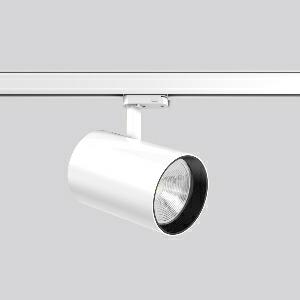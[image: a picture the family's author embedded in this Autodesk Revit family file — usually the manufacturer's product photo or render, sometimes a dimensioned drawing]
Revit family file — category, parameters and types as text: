
# Revit family: deecos_s_maxi_742231_002_76_5936
name_source: partatom
category: Lighting Fixtures
units: mm (PartAtom-declared; Revit-internal decimal feet)

## family parameters
Cut with Voids When Loaded = No
Host = Face
Light Source = No
Part Type = Normal
Room Calculation Point = No
Round Connector Dimension = Use Diameter
Shared = No

## types (1)
- DEECOS S maxi (1 x LED Modul 932 fresh meat, 1800 lm, 3200)
    Apparent Load = 33 VA
    Approval mark = CE
    CIE Flux Codes = 97 100 100 100 100
    Color Rendering = 90
    Color Temperature = 3200
    Default Elevation = 1800 mm  [stored 5.90551 ft]
    Description = Series: DEECOS S maxi
LED surface-mounted projector in modern design with no visible cooling ribs. Housing: die-cast aluminium, powder-coated. Rotation range: 356°. Swivel range: 90°. Black plastic ring and recessed LED to prevent glare from the side. Optical assembly with lens made of plastic (polycarbonate) for the best homogeneous light distribution - can be changed without tools. Special LED for illumination of meat included. With adapter for RZB 3-circuit DALI tracks. Suitable for Track on ceiling, Wall track. High quality converter without flickering and stroboscopic effect. The following accessories can be mounted without use of tools: interchangeable lenses, decorative glasses, honeycomb louvre, clear and frosted diffusers, white interchangeable plastic ring. 
Colour: traffic white, matt (RAL 9016)
Diameter: 123 mm
Height: 200 mm
Lamp: LED
Socket: without socket
Colour temperature: fresh meat
System power: 33 W
Rated luminous flux: 1800 lm
Luminous efficiency: 55 lm/W
Control gear: Converter, dimmable, DALI
Protection class: I
Type of protection: IP 20
    Height = 200 mm  [stored 0.656168 ft]
    Lamp = 1 x LED Modul 932 fresh meat
    Lamp Light Flux = 1800 lm
    Lamp count = 1
    Length = 123 mm
    Lifetime = 50000 h
    Luminous efficacy = 55 lm/W
    Manufacturer = RZB
    ModVariant = No
    Model = 742231.002.76
    Mounting Place = Ceiling
    Mounting Type = Rail mounted
    Number of Poles = 1
    OnlyDefault = Yes
    Power Factor = 1
    Product Name = DEECOS S maxi
    Product group = Track mounted projectors
    ProductGroupID = 301
    Protection Class = Protection class I
    Protection Degree = IP 20
    RLX_Detail_Level = 1
    RLX_Emergency_Light_Flux = 0 lm
    RLX_Emergency_Type = 0
    RLX_Emergency_Type_DB = No
    RlxData = <blob elided: 39117 chars, md5=d051820e>
    Socket = socket
    Standby Power = 0 W
    System Light Flux = 1800 lm
    System Power = 33 W
    Type Comments = Product without accessories
    Type Image = 741958.002.jpg
    URL = http://relux.com
    VarID = ---
    Voltage = 230 V
    Voltage Range = 220-240 V
    Weight = 0.00 kg
    Width = 0 mm  [stored 0 ft]

note: [stored X ft] marks values corroborated as IEEE doubles in the binary element streams (Revit-internal decimal feet)

## geometry (parser evidence)
native form markers: Blend x4, Sweep x13
no freeform markers — native parametric forms only
